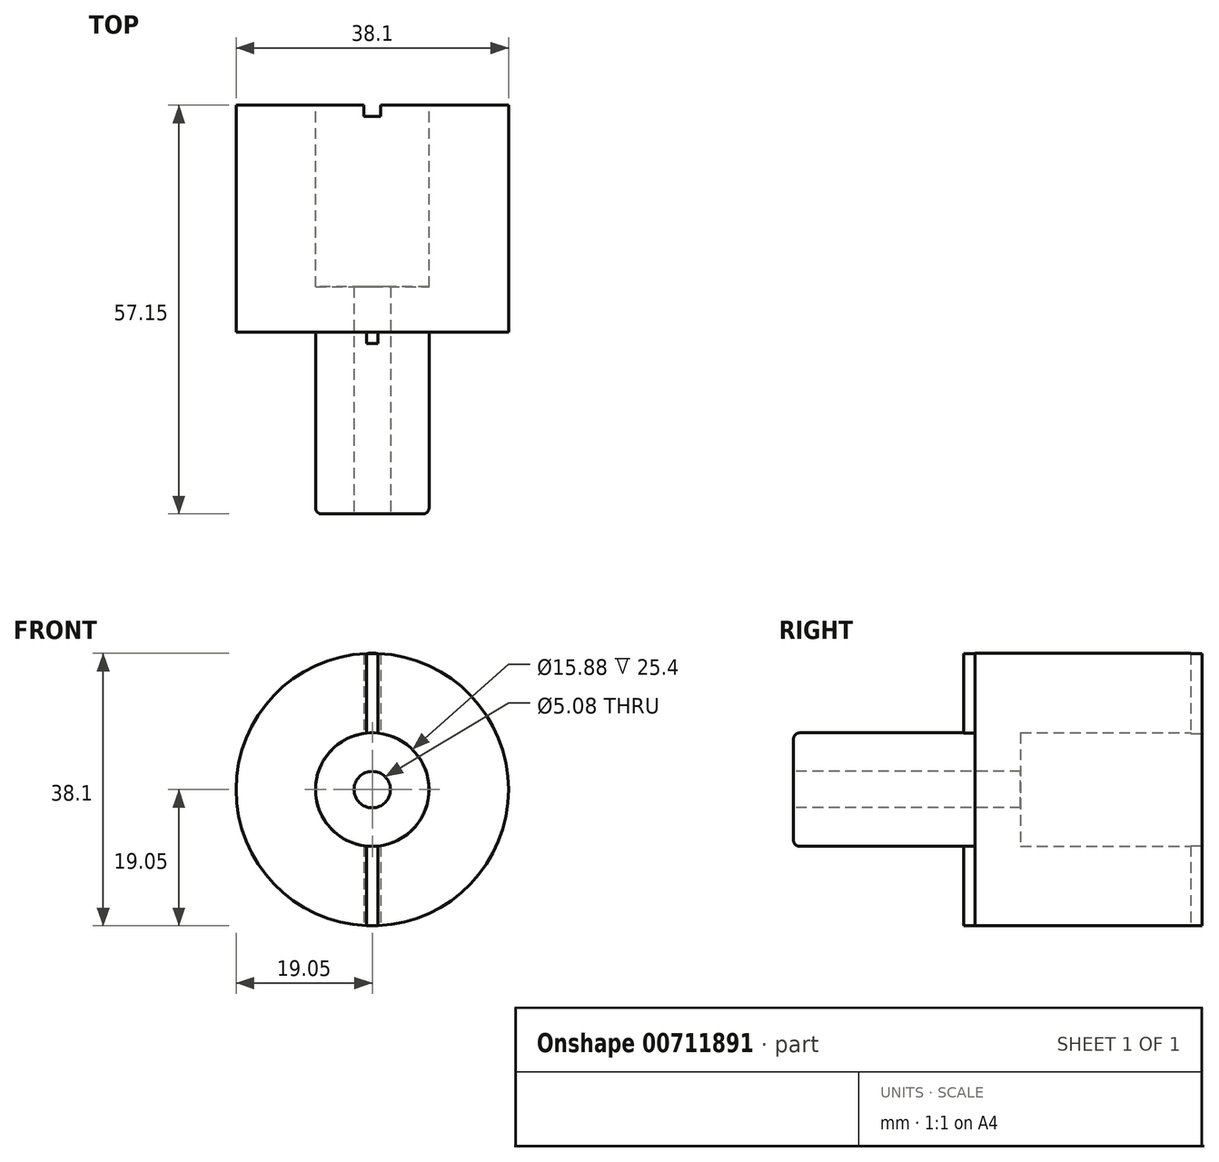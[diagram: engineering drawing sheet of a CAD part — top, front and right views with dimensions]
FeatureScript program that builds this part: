
annotation { "Feature Type Name" : "Feature", "Feature Type Description" : "" }
export const myFeature = defineFeature(function(context is Context, id is Id, definition is map)
    precondition{}
    {
        {
            var Q0;
            Q0=qCreatedBy(makeId("Front.planeOp"),FACE);
            var sketch = newSketch(context, id + "F0", { "sketchPlane" : qUnion([Q0])});
            skCircle(sketch, "E0", {"center": v(0, 0) * mm, "radius": 19.05 * mm});
            skSolve(sketch);
        }
        {
            var Q0;
            Q0=makeQuery(id+"F0.imprint","IMPRINT",FACE,{"disambiguationData":[TD([[makeQuery(id+"F0.imprint","IMPRINT",EDGE,{"derivedFrom":sQuery(id+"F0.wireOp",EDGE,"E0")}),1.0]])]});
            extrude(context, id + "F1", {"entities" : qUnion([Q0]), "depth" : 31.75 * mm, "offsetDistance" : 25.4 * mm});
        }
        {
            var Q0;
            Q0=makeQuery(id+"F1.opExtrude","CAP_FACE",FACE,{"disambiguationData":[OSD([sQuery(id+"F0.wireOp",EDGE,"E0")])],"isStart":false});
            var sketch = newSketch(context, id + "F2", { "sketchPlane" : qUnion([Q0])});
            skCircle(sketch, "E1", {"center": v(0, 0) * mm, "radius": 7.94 * mm});
            skSolve(sketch);
        }
        {
            var Q0;
            Q0=makeQuery(id+"F2.imprint","IMPRINT",FACE,{"disambiguationData":[TD([[makeQuery(id+"F2.imprint","IMPRINT",EDGE,{"derivedFrom":sQuery(id+"F2.wireOp",EDGE,"E1")}),1.0]])]});
            extrude(context, id + "F3", {"entities" : qUnion([Q0]), "operationType" : NewBodyOperationType.ADD, "depth" : 25.4 * mm, "offsetDistance" : 25.4 * mm});
        }
        {
            var Q0;
            Q0=makeQuery(id+"F3.opExtrude","CAP_EDGE",EDGE,{"disambiguationData":[OSD([sQuery(id+"F2.wireOp",EDGE,"E1")])],"isStart":false});
            fillet(context, id + "F4", {"entities" : qUnion([Q0]), "radius" : 0.86 * mm, "tangentPropagation" : true, "allowEdgeOverflow" : false});
        }
        {
            var Q0;
            Q0=makeQuery(id+"F1.opExtrude","CAP_FACE",FACE,{"disambiguationData":[OSD([sQuery(id+"F0.wireOp",EDGE,"E0")])],"isStart":false});
            var sketch = newSketch(context, id + "F5", { "sketchPlane" : qUnion([Q0])});
            skLineSegment(sketch, "E2.bottom", {"start": v(-0.8, 19.03) * mm, "end": v(0.8, 19.03) * mm});
            skLineSegment(sketch, "E2.top", {"start": v(-0.8, -19.03) * mm, "end": v(0.8, -19.03) * mm});
            skLineSegment(sketch, "E2.left", {"start": v(-0.8, 19.03) * mm, "end": v(-0.8, -19.03) * mm});
            skLineSegment(sketch, "E2.right", {"start": v(0.8, 19.03) * mm, "end": v(0.8, -19.03) * mm});
            skPoint(sketch, "E2.middle", {"position": v(0, 0) * mm});
            skSolve(sketch);
        }
        {
            var Q0;
            {var subQ0=sQuery(id+"F5.wireOp",EDGE,"E2.bottom");Q0=makeQuery(id+"F5.imprint","IMPRINT",FACE,{"disambiguationData":[TD([[makeQuery(id+"F5.imprint","IMPRINT",EDGE,{"derivedFrom":subQ0}),-1.0]])]});}
            extrude(context, id + "F6", {"entities" : qUnion([Q0]), "operationType" : NewBodyOperationType.ADD, "depth" : 1.59 * mm, "offsetDistance" : 25.4 * mm});
        }
        {
            var Q0;
            {var subQ0=sQuery(id+"F0.wireOp",EDGE,"E0");var subQ1=makeQuery(id+"F1.opExtrude","CAP_FACE",FACE,{"disambiguationData":[OSD([subQ0])],"isStart":false});Q0=makeQuery(id+"F6.boolean.opBoolean","SPLIT",FACE,{"disambiguationData":[TD([makeQuery(id+"F1.opExtrude","SWEPT_FACE",FACE,{"disambiguationData":[OSD([subQ0])]}),subQ1,makeQuery(id+"F3.opExtrude","SWEPT_FACE",FACE,{"disambiguationData":[OSD([sQuery(id+"F2.wireOp",EDGE,"E1")])]}),makeQuery(id+"F6.opExtrude","SWEPT_FACE",FACE,{"disambiguationData":[OSD([sQuery(id+"F5.wireOp",EDGE,"E2.bottom")])]}),makeQuery(id+"F6.opExtrude","SWEPT_FACE",FACE,{"disambiguationData":[OSD([sQuery(id+"F5.wireOp",EDGE,"E2.left")])]}),makeQuery(id+"F6.opExtrude","SWEPT_FACE",FACE,{"disambiguationData":[OSD([sQuery(id+"F5.wireOp",EDGE,"E2.right")])]})])],"derivedFrom":subQ1});}
            var sketch = newSketch(context, id + "F7", { "sketchPlane" : qUnion([Q0])});
            skLineSegment(sketch, "E3.bottom", {"start": v(-0.8, -19.03) * mm, "end": v(0.8, -19.03) * mm});
            skLineSegment(sketch, "E3.top", {"start": v(-0.8, 19.03) * mm, "end": v(0.8, 19.03) * mm});
            skLineSegment(sketch, "E3.left", {"start": v(-0.8, -19.03) * mm, "end": v(-0.8, 19.03) * mm});
            skLineSegment(sketch, "E3.right", {"start": v(0.8, -19.03) * mm, "end": v(0.8, 19.03) * mm});
            skPoint(sketch, "E3.middle", {"position": v(0, 0) * mm});
            skSolve(sketch);
        }
        {
            var Q0;
            {var subQ0=sQuery(id+"F7.wireOp",EDGE,"E3.bottom");Q0=makeQuery(id+"F7.imprint","IMPRINT",FACE,{"disambiguationData":[TD([[makeQuery(id+"F7.imprint","IMPRINT",EDGE,{"derivedFrom":subQ0}),1.0]])]});}
            extrude(context, id + "F8", {"entities" : qUnion([Q0]), "operationType" : NewBodyOperationType.ADD, "depth" : 1.59 * mm, "offsetDistance" : 25.4 * mm});
        }
        {
            var Q0;
            Q0=makeQuery(id+"F3.opExtrude","CAP_FACE",FACE,{"disambiguationData":[OSD([sQuery(id+"F2.wireOp",EDGE,"E1")])],"isStart":false});
            var sketch = newSketch(context, id + "F9", { "sketchPlane" : qUnion([Q0])});
            skCircle(sketch, "E4", {"center": v(0, 0) * mm, "radius": 2.54 * mm});
            skSolve(sketch);
        }
        {
            var Q0;
            Q0=makeQuery(id+"F1.opExtrude","CAP_FACE",FACE,{"disambiguationData":[OSD([sQuery(id+"F0.wireOp",EDGE,"E0")])],"isStart":true});
            var sketch = newSketch(context, id + "F10", { "sketchPlane" : qUnion([Q0])});
            skLineSegment(sketch, "E5.bottom", {"start": v(-1.16, 20.32) * mm, "end": v(1.16, 20.32) * mm});
            skLineSegment(sketch, "E5.top", {"start": v(-1.16, -20.32) * mm, "end": v(1.16, -20.32) * mm});
            skLineSegment(sketch, "E5.left", {"start": v(-1.16, 20.32) * mm, "end": v(-1.16, -20.32) * mm});
            skLineSegment(sketch, "E5.right", {"start": v(1.16, 20.32) * mm, "end": v(1.16, -20.32) * mm});
            skPoint(sketch, "E5.middle", {"position": v(0, 0) * mm});
            skSolve(sketch);
        }
        {
            var Q0;
            {var subQ0=sQuery(id+"F10.wireOp",EDGE,"E5.left");var subQ1=makeQuery(id+"F1.opExtrude","CAP_EDGE",EDGE,{"disambiguationData":[OSD([sQuery(id+"F0.wireOp",EDGE,"E0")])],"isStart":true});var subQ2=makeQuery(id+"F10.imprint","INTERSECT",VERTEX,{"disambiguationData":[OD(0.0)],"derivedFrom":[subQ1,subQ0]});Q0=makeQuery(id+"F10.imprint","IMPRINT",FACE,{"disambiguationData":[TD([[makeQuery(id+"F10.imprint","IMPRINT",EDGE,{"disambiguationData":[TD([[subQ2,-1.0]])],"derivedFrom":subQ0}),1.0]])]});}
            var sketch = newSketch(context, id + "F11", { "sketchPlane" : qUnion([Q0])});
            skCircle(sketch, "E6", {"center": v(0, 0) * mm, "radius": 7.94 * mm});
            skSolve(sketch);
        }
        {
            var Q0;
            Q0 = qSketchRegion(id + "F11", true);
            extrude(context, id + "F12", {"entities" : qUnion([Q0]), "operationType" : NewBodyOperationType.REMOVE, "oppositeDirection" : true, "depth" : 25.4 * mm, "offsetDistance" : 25.4 * mm});
        }
        {
            var Q0;
            Q0 = qSketchRegion(id + "F9", true);
            extrude(context, id + "F13", {"entities" : qUnion([Q0]), "operationType" : NewBodyOperationType.REMOVE, "oppositeDirection" : true, "depth" : 31.75 * mm, "offsetDistance" : 25.4 * mm});
        }
        {
            var Q0;
            {var subQ0=sQuery(id+"F10.wireOp",EDGE,"E5.left");var subQ1=makeQuery(id+"F1.opExtrude","CAP_EDGE",EDGE,{"disambiguationData":[OSD([sQuery(id+"F0.wireOp",EDGE,"E0")])],"isStart":true});var subQ2=makeQuery(id+"F10.imprint","INTERSECT",VERTEX,{"disambiguationData":[OD(0.0)],"derivedFrom":[subQ1,subQ0]});Q0=makeQuery(id+"F10.imprint","IMPRINT",FACE,{"disambiguationData":[TD([[makeQuery(id+"F10.imprint","IMPRINT",EDGE,{"disambiguationData":[TD([[subQ2,-1.0]])],"derivedFrom":subQ0}),1.0]])]});}
            extrude(context, id + "F14", {"entities" : qUnion([Q0]), "operationType" : NewBodyOperationType.REMOVE, "oppositeDirection" : true, "depth" : 1.59 * mm, "offsetDistance" : 25.4 * mm});
        }
    });
